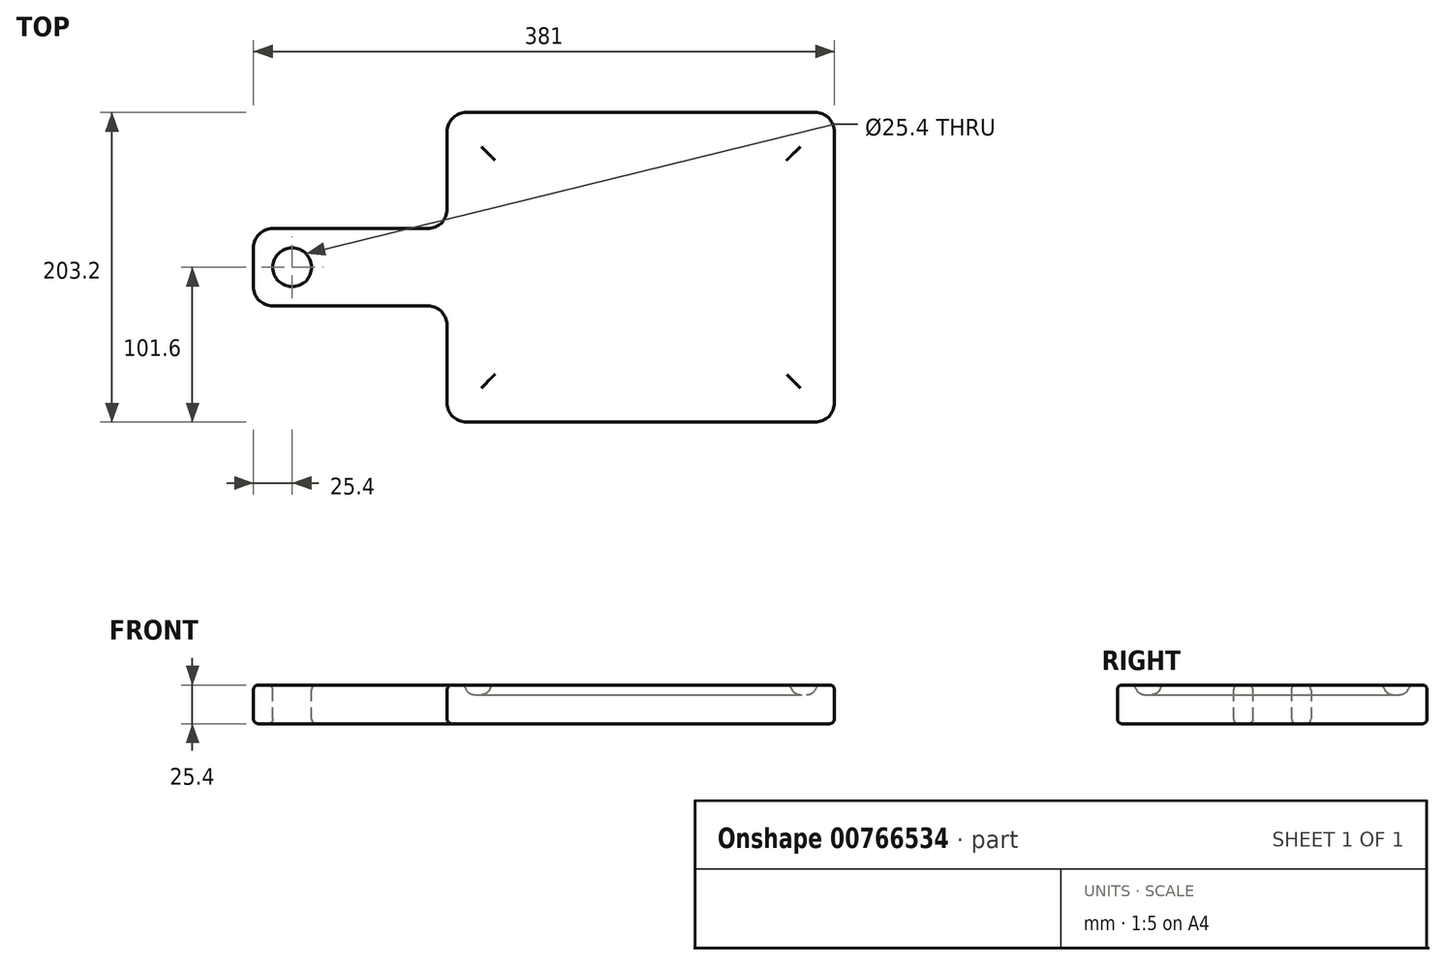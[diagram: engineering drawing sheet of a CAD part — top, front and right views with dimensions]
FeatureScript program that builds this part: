
annotation { "Feature Type Name" : "Feature", "Feature Type Description" : "" }
export const myFeature = defineFeature(function(context is Context, id is Id, definition is map)
    precondition{}
    {
        {
            var Q0;
            Q0=qCreatedBy(makeId("Top.planeOp"),FACE);
            var sketch = newSketch(context, id + "F0", { "sketchPlane" : qUnion([Q0])});
            skLineSegment(sketch, "E0.bottom", {"start": v(0, 0) * mm, "end": v(254, 0) * mm});
            skLineSegment(sketch, "E0.top", {"start": v(0, 203.2) * mm, "end": v(254, 203.2) * mm});
            skLineSegment(sketch, "E0.left", {"start": v(0, 0) * mm, "end": v(0, 203.2) * mm});
            skLineSegment(sketch, "E0.right", {"start": v(254, 0) * mm, "end": v(254, 203.2) * mm});
            skLineSegment(sketch, "E1.bottom", {"start": v(0, 76.2) * mm, "end": v(-127, 76.2) * mm});
            skLineSegment(sketch, "E1.top", {"start": v(0, 127) * mm, "end": v(-127, 127) * mm});
            skLineSegment(sketch, "E1.left", {"start": v(0, 76.2) * mm, "end": v(0, 127) * mm});
            skLineSegment(sketch, "E1.right", {"start": v(-127, 76.2) * mm, "end": v(-127, 127) * mm});
            skSolve(sketch);
        }
        {
            var Q0;
            {var subQ3=sQuery(id+"F0.wireOp",EDGE,"E0.bottom");Q0=makeQuery(id+"F0.imprint","IMPRINT",FACE,{"disambiguationData":[TD([[makeQuery(id+"F0.imprint","IMPRINT",EDGE,{"derivedFrom":subQ3}),1.0]])]});}
            var Q1;
            Q1=makeQuery(id+"F0.imprint","IMPRINT",FACE,{"disambiguationData":[TD([[makeQuery(id+"F0.imprint","IMPRINT",EDGE,{"derivedFrom":sQuery(id+"F0.wireOp",EDGE,"E1.bottom")}),-1.0]])]});
            extrude(context, id + "F1", {"entities" : qUnion([Q0, Q1]), "depth" : 25.4 * mm, "offsetDistance" : 25.4 * mm});
        }
        {
            var Q0;
            Q0=makeQuery(id+"F1.opExtrude","CAP_FACE",FACE,{"disambiguationData":[OSD([sQuery(id+"F0.wireOp",EDGE,"E0.bottom"),sQuery(id+"F0.wireOp",EDGE,"E0.top"),sQuery(id+"F0.wireOp",EDGE,"E0.left"),sQuery(id+"F0.wireOp",EDGE,"E0.right"),sQuery(id+"F0.wireOp",EDGE,"E1.bottom"),sQuery(id+"F0.wireOp",EDGE,"E1.top"),sQuery(id+"F0.wireOp",EDGE,"E1.right")])],"isStart":false});
            var sketch = newSketch(context, id + "F2", { "sketchPlane" : qUnion([Q0])});
            skCircle(sketch, "E2", {"center": v(-101.6, 101.6) * mm, "radius": 12.7 * mm});
            skSolve(sketch);
        }
        {
            var Q0;
            Q0 = qSketchRegion(id + "F2", true);
            var Q1;
            Q1=sQuery(id+"F2.wireOp",EDGE,"E2");
            extrude(context, id + "F3", {"entities" : qUnion([Q0]), "operationType" : NewBodyOperationType.REMOVE, "surfaceEntities" : qUnion([Q1]), "oppositeDirection" : true, "depth" : 25.4 * mm, "offsetDistance" : 25.4 * mm});
        }
        {
            var Q0;
            Q0=makeQuery(id+"F1.opExtrude","CAP_FACE",FACE,{"disambiguationData":[OSD([sQuery(id+"F0.wireOp",EDGE,"E0.bottom"),sQuery(id+"F0.wireOp",EDGE,"E0.top"),sQuery(id+"F0.wireOp",EDGE,"E0.left"),sQuery(id+"F0.wireOp",EDGE,"E0.right"),sQuery(id+"F0.wireOp",EDGE,"E1.bottom"),sQuery(id+"F0.wireOp",EDGE,"E1.top"),sQuery(id+"F0.wireOp",EDGE,"E1.right")])],"isStart":false});
            var sketch = newSketch(context, id + "F4", { "sketchPlane" : qUnion([Q0])});
            skLineSegment(sketch, "E3.0", {"start": v(11.68, 11.68) * mm, "end": v(11.68, 76.2) * mm});
            skLineSegment(sketch, "E3.1", {"start": v(11.68, 127) * mm, "end": v(11.68, 191.52) * mm});
            skLineSegment(sketch, "E3.2", {"start": v(11.68, 191.52) * mm, "end": v(242.32, 191.52) * mm});
            skLineSegment(sketch, "E3.3", {"start": v(242.32, 11.68) * mm, "end": v(242.32, 191.52) * mm});
            skLineSegment(sketch, "E3.4", {"start": v(11.68, 11.68) * mm, "end": v(242.32, 11.68) * mm});
            skLineSegment(sketch, "E4", {"start": v(11.68, 127) * mm, "end": v(11.68, 76.2) * mm});
            skLineSegment(sketch, "E5.0", {"start": v(28.7, 127) * mm, "end": v(28.7, 174.5) * mm});
            skLineSegment(sketch, "E5.1", {"start": v(225.3, 28.7) * mm, "end": v(225.3, 174.5) * mm});
            skLineSegment(sketch, "E5.2", {"start": v(28.7, 28.7) * mm, "end": v(225.3, 28.7) * mm});
            skLineSegment(sketch, "E5.3", {"start": v(28.7, 174.5) * mm, "end": v(225.3, 174.5) * mm});
            skLineSegment(sketch, "E5.4", {"start": v(28.7, 28.7) * mm, "end": v(28.7, 76.2) * mm});
            skLineSegment(sketch, "E5.5", {"start": v(28.7, 127) * mm, "end": v(28.7, 76.2) * mm});
            skSolve(sketch);
        }
        {
            var Q0;
            Q0=makeQuery(id+"F4.imprint","IMPRINT",FACE,{"disambiguationData":[TD([[makeQuery(id+"F4.imprint","IMPRINT",EDGE,{"derivedFrom":sQuery(id+"F4.wireOp",EDGE,"E3.0")}),-1.0]])]});
            extrude(context, id + "F5", {"entities" : qUnion([Q0]), "operationType" : NewBodyOperationType.REMOVE, "oppositeDirection" : true, "depth" : 6.35 * mm, "offsetDistance" : 25.4 * mm});
        }
        {
            var Q0;
            Q0=makeQuery(id+"F5.boolean.opBoolean","COPY",FACE,{"derivedFrom":makeQuery(id+"F5.opExtrude","CAP_FACE",FACE,{"disambiguationData":[OSD([sQuery(id+"F4.wireOp",EDGE,"E3.0"),sQuery(id+"F4.wireOp",EDGE,"E3.1"),sQuery(id+"F4.wireOp",EDGE,"E3.2"),sQuery(id+"F4.wireOp",EDGE,"E3.3"),sQuery(id+"F4.wireOp",EDGE,"E3.4"),sQuery(id+"F4.wireOp",EDGE,"E4"),sQuery(id+"F4.wireOp",EDGE,"E5.0"),sQuery(id+"F4.wireOp",EDGE,"E5.1"),sQuery(id+"F4.wireOp",EDGE,"E5.2"),sQuery(id+"F4.wireOp",EDGE,"E5.3"),sQuery(id+"F4.wireOp",EDGE,"E5.4"),sQuery(id+"F4.wireOp",EDGE,"E5.5")])],"isStart":false})});
            fillet(context, id + "F6", {"entities" : qUnion([Q0]), "radius" : 6.35 * mm, "tangentPropagation" : true, "allowEdgeOverflow" : false});
        }
        {
            var Q0;
            Q0=makeQuery(id+"F6.opFillet","BLEND_EDGE",EDGE,{"blendedFrom":[makeQuery(id+"F5.boolean.opBoolean","COPY",EDGE,{"derivedFrom":makeQuery(id+"F5.opExtrude","CAP_EDGE",EDGE,{"disambiguationData":[OSD([sQuery(id+"F4.wireOp",EDGE,"E3.0"),sQuery(id+"F4.wireOp",EDGE,"E3.1"),sQuery(id+"F4.wireOp",EDGE,"E4")])],"isStart":false})}),makeQuery(id+"F5.boolean.opBoolean","COPY",EDGE,{"derivedFrom":makeQuery(id+"F5.opExtrude","CAP_EDGE",EDGE,{"disambiguationData":[OSD([sQuery(id+"F4.wireOp",EDGE,"E3.2")])],"isStart":false})})],"blendedInto":[]});
            var Q1;
            Q1=makeQuery(id+"F6.opFillet","BLEND_EDGE",EDGE,{"blendedFrom":[makeQuery(id+"F5.boolean.opBoolean","COPY",EDGE,{"derivedFrom":makeQuery(id+"F5.opExtrude","CAP_EDGE",EDGE,{"disambiguationData":[OSD([sQuery(id+"F4.wireOp",EDGE,"E3.2")])],"isStart":false})}),makeQuery(id+"F5.boolean.opBoolean","COPY",EDGE,{"derivedFrom":makeQuery(id+"F5.opExtrude","CAP_EDGE",EDGE,{"disambiguationData":[OSD([sQuery(id+"F4.wireOp",EDGE,"E3.3")])],"isStart":false})})],"blendedInto":[]});
            var Q2;
            Q2=makeQuery(id+"F6.opFillet","BLEND_EDGE",EDGE,{"blendedFrom":[makeQuery(id+"F5.boolean.opBoolean","COPY",EDGE,{"derivedFrom":makeQuery(id+"F5.opExtrude","CAP_EDGE",EDGE,{"disambiguationData":[OSD([sQuery(id+"F4.wireOp",EDGE,"E3.0"),sQuery(id+"F4.wireOp",EDGE,"E3.1"),sQuery(id+"F4.wireOp",EDGE,"E4")])],"isStart":false})}),makeQuery(id+"F5.boolean.opBoolean","COPY",EDGE,{"derivedFrom":makeQuery(id+"F5.opExtrude","CAP_EDGE",EDGE,{"disambiguationData":[OSD([sQuery(id+"F4.wireOp",EDGE,"E3.4")])],"isStart":false})})],"blendedInto":[]});
            var Q3;
            Q3=makeQuery(id+"F6.opFillet","BLEND_EDGE",EDGE,{"blendedFrom":[makeQuery(id+"F5.boolean.opBoolean","COPY",EDGE,{"derivedFrom":makeQuery(id+"F5.opExtrude","CAP_EDGE",EDGE,{"disambiguationData":[OSD([sQuery(id+"F4.wireOp",EDGE,"E3.3")])],"isStart":false})}),makeQuery(id+"F5.boolean.opBoolean","COPY",EDGE,{"derivedFrom":makeQuery(id+"F5.opExtrude","CAP_EDGE",EDGE,{"disambiguationData":[OSD([sQuery(id+"F4.wireOp",EDGE,"E3.4")])],"isStart":false})})],"blendedInto":[]});
            fillet(context, id + "F7", {"entities" : qUnion([Q0, Q1, Q2, Q3]), "radius" : 6.35 * mm, "tangentPropagation" : true, "allowEdgeOverflow" : false});
        }
        {
            var Q0;
            Q0=makeQuery(id+"F1.opExtrude","SWEPT_EDGE",EDGE,{"disambiguationData":[OSD([sQuery(id+"F0.wireOp",EDGE,"E0.bottom"),sQuery(id+"F0.wireOp",EDGE,"E0.right")])]});
            var Q1;
            Q1=makeQuery(id+"F1.opExtrude","SWEPT_EDGE",EDGE,{"disambiguationData":[OSD([sQuery(id+"F0.wireOp",EDGE,"E0.top"),sQuery(id+"F0.wireOp",EDGE,"E0.right")])]});
            var Q2;
            Q2=makeQuery(id+"F1.opExtrude","SWEPT_EDGE",EDGE,{"disambiguationData":[OSD([sQuery(id+"F0.wireOp",EDGE,"E0.bottom"),sQuery(id+"F0.wireOp",EDGE,"E0.left")])]});
            var Q3;
            Q3=makeQuery(id+"F1.opExtrude","SWEPT_EDGE",EDGE,{"disambiguationData":[OSD([sQuery(id+"F0.wireOp",EDGE,"E0.top"),sQuery(id+"F0.wireOp",EDGE,"E0.left")])]});
            var Q4;
            Q4=makeQuery(id+"F1.opExtrude","SWEPT_EDGE",EDGE,{"disambiguationData":[OSD([sQuery(id+"F0.wireOp",EDGE,"E1.bottom"),sQuery(id+"F0.wireOp",EDGE,"E1.right")])]});
            var Q5;
            Q5=makeQuery(id+"F1.opExtrude","SWEPT_EDGE",EDGE,{"disambiguationData":[OSD([sQuery(id+"F0.wireOp",EDGE,"E1.top"),sQuery(id+"F0.wireOp",EDGE,"E1.right")])]});
            var Q6;
            Q6=makeQuery(id+"F1.opExtrude","SWEPT_EDGE",EDGE,{"disambiguationData":[OSD([sQuery(id+"F0.wireOp",EDGE,"E0.left"),sQuery(id+"F0.wireOp",EDGE,"E1.top"),sQuery(id+"F0.wireOp",EDGE,"E1.left")])]});
            var Q7;
            Q7=makeQuery(id+"F1.opExtrude","SWEPT_EDGE",EDGE,{"disambiguationData":[OSD([sQuery(id+"F0.wireOp",EDGE,"E0.left"),sQuery(id+"F0.wireOp",EDGE,"E1.bottom"),sQuery(id+"F0.wireOp",EDGE,"E1.left")])]});
            fillet(context, id + "F8", {"entities" : qUnion([Q0, Q1, Q2, Q3, Q4, Q5, Q6, Q7]), "radius" : 12.7 * mm, "tangentPropagation" : true, "allowEdgeOverflow" : false});
        }
        {
            var Q0;
            Q0=makeQuery(id+"F5.boolean.opBoolean","SPLIT",FACE,{"disambiguationData":[TD([makeQuery(id+"F5.opExtrude","SWEPT_FACE",FACE,{"disambiguationData":[OSD([sQuery(id+"F4.wireOp",EDGE,"E5.1")])]})])],"derivedFrom":makeQuery(id+"F1.opExtrude","CAP_FACE",FACE,{"disambiguationData":[OSD([sQuery(id+"F0.wireOp",EDGE,"E0.bottom"),sQuery(id+"F0.wireOp",EDGE,"E0.top"),sQuery(id+"F0.wireOp",EDGE,"E0.left"),sQuery(id+"F0.wireOp",EDGE,"E0.right"),sQuery(id+"F0.wireOp",EDGE,"E1.bottom"),sQuery(id+"F0.wireOp",EDGE,"E1.top"),sQuery(id+"F0.wireOp",EDGE,"E1.right")])],"isStart":false})});
            var Q1;
            {var subQ0=sQuery(id+"F0.wireOp",EDGE,"E1.right");var subQ1=sQuery(id+"F0.wireOp",EDGE,"E1.top");var subQ2=sQuery(id+"F0.wireOp",EDGE,"E1.bottom");var subQ3=sQuery(id+"F0.wireOp",EDGE,"E0.right");var subQ4=sQuery(id+"F0.wireOp",EDGE,"E0.bottom");var subQ5=sQuery(id+"F0.wireOp",EDGE,"E0.left");var subQ6=sQuery(id+"F0.wireOp",EDGE,"E0.top");Q1=makeQuery(id+"F5.boolean.opBoolean","SPLIT",FACE,{"disambiguationData":[TD([makeQuery(id+"F1.opExtrude","SWEPT_FACE",FACE,{"disambiguationData":[OSD([subQ4])]})])],"derivedFrom":makeQuery(id+"F1.opExtrude","CAP_FACE",FACE,{"disambiguationData":[OSD([subQ4,subQ6,subQ5,subQ3,subQ2,subQ1,subQ0])],"isStart":false})});}
            var Q2;
            Q2=makeQuery(id+"F1.opExtrude","CAP_FACE",FACE,{"disambiguationData":[OSD([sQuery(id+"F0.wireOp",EDGE,"E0.bottom"),sQuery(id+"F0.wireOp",EDGE,"E0.top"),sQuery(id+"F0.wireOp",EDGE,"E0.left"),sQuery(id+"F0.wireOp",EDGE,"E0.right"),sQuery(id+"F0.wireOp",EDGE,"E1.bottom"),sQuery(id+"F0.wireOp",EDGE,"E1.top"),sQuery(id+"F0.wireOp",EDGE,"E1.right")])],"isStart":true});
            fillet(context, id + "F9", {"entities" : qUnion([Q0, Q1, Q2]), "radius" : 3.17 * mm, "tangentPropagation" : true, "allowEdgeOverflow" : false});
        }
    });
